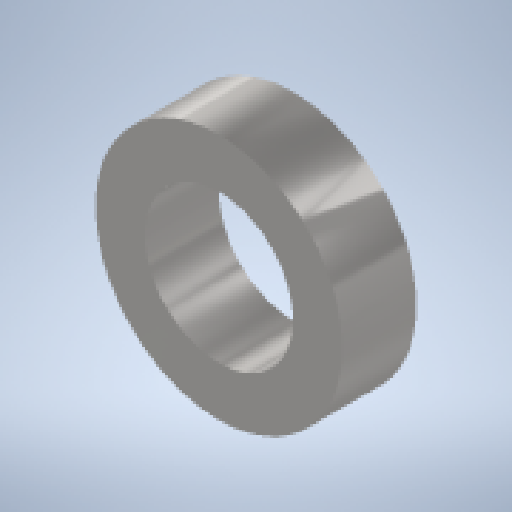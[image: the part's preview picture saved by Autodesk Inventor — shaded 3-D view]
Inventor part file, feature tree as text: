
AUTODESK INVENTOR PART (.ipt)
format: ipt  version: 2024 (Build 280153000, 153)  size: 141,312 bytes
history: native  units: mm
features: other x1, extrude x1, sketch x1
ambient origin geometry x8: Origin, YZ Plane, XZ Plane, XY Plane, X Axis, Y Axis, Z Axis, Center Point
bodies: Body1 (feature_tree)
feature tree (3):
  other  "ソリッド1"
  extrude  "押し出し1"  Depth=6.0mm
  sketch  "スケッチ1"
